# Revit family: MI-ROC
name_source: partatom
category: Pipe Accessories
revit_build: Autodesk Revit 2018 (Build: 20170223_1515(x64)
units: mm (PartAtom-declared; Revit-internal decimal feet)

## family parameters
Always vertical = Yes
Cut with Voids When Loaded = No
Part Type = Normal
Round Connector Dimension = Use Diameter
Shared = No
Work Plane-Based = No

## types (12) — shared parameters
Description = HYDRO MECHANICAL GREASE INTERCEPTOR WITH THREE WAY OUTLET
Manufacturer = MIFAB
URL = WWW.MIFAB.COM

## per-type parameters (varying)
| type | A-Width | B-Length | C-Pipe Offset | E-Height | F-Dia |
| MI-ROC-1 | 0' - 9 1/4" | 0' - 6 1/4" | 0' - 3 1/2" | 0' - 9" | 0' - 1 1/2" |
| MI-ROC-2 | 0' - 10 1/4" | 0' - 8 1/4" | 0' - 3 7/8" | 0' - 11 1/2" | 0' - 2" |
| MI-ROC-3 | 1' - 0 3/4" | 0' - 10 1/4" | 0' - 4 1/2" | 1' - 0 7/8" | 0' - 2" |
| MI-ROC-4 | 1' - 6 1/2" | 0' - 10 1/4" | 0' - 4 7/8" | 1' - 3 7/8" | 0' - 2" |
| MI-ROC-5 | 1' - 8 1/4" | 1' - 2 1/4" | 0' - 5 7/8" | 1' - 5 7/8" | 0' - 2" |
| MI-ROC-6 | 2' - 0 1/2" | 1' - 6 1/4" | 0' - 6 1/8" | 1' - 8 5/8" | 0' - 3" |
| MI-ROC-7 | 2' - 0 1/2" | 1' - 6 1/4" | 0' - 8 5/8" | 2' - 1 1/8" | 0' - 3" |
| MI-ROC-8 | 2' - 2 1/4" | 1' - 8 1/4" | 0' - 7 7/8" | 2' - 5 3/8" | 0' - 4" |
| MI-ROC-9 | 2' - 5 1/2" | 1' - 8 1/4" | 0' - 8 3/8" | 2' - 5 3/8" | 0' - 4" |
| MI-ROC-10 | 2' - 9" | 1' - 8 1/4" | 0' - 7 7/8" | 2' - 5 3/8" | 0' - 4" |
| MI-ROC-11 | 2' - 9" | 1' - 10 3/4" | 0' - 8 1/2" | 2' - 6 1/2" | 0' - 4" |
| MI-ROC-12 | 2' - 11 1/2" | 2' - 6" | 0' - 8 1/8" | 2' - 6 1/8" | 0' - 4" |

note: column(s) folded — value = type name in every type: Model

## geometry (parser evidence)
native form markers: Sweep x10
no freeform markers — native parametric forms only
